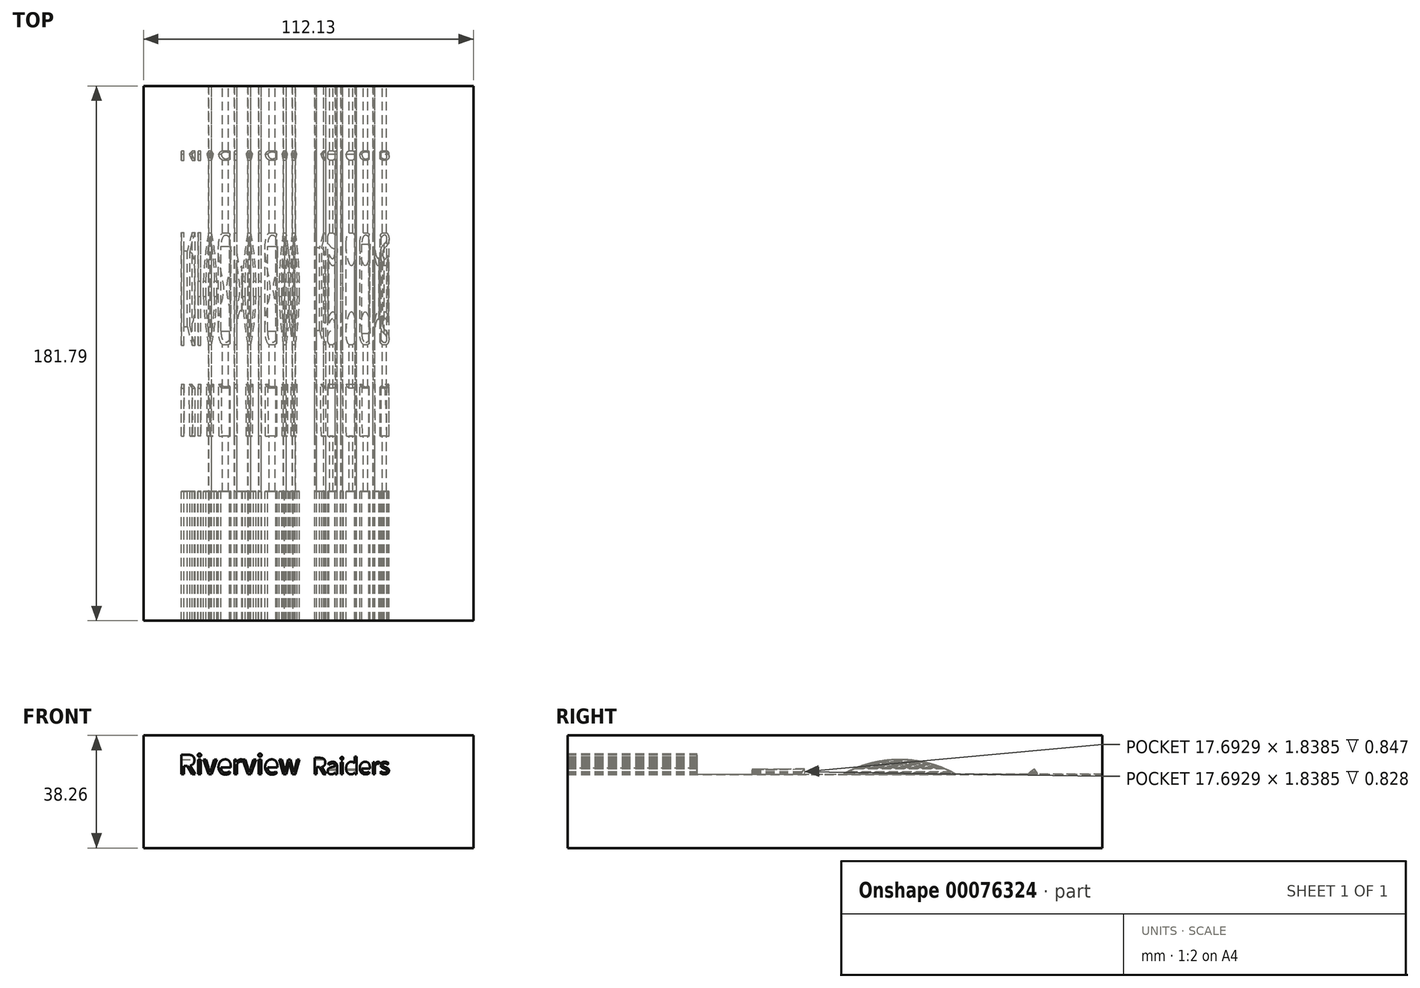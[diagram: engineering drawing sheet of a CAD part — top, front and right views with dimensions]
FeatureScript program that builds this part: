
annotation { "Feature Type Name" : "Feature", "Feature Type Description" : "" }
export const myFeature = defineFeature(function(context is Context, id is Id, definition is map)
    precondition{}
    {
        {
            var Q0;
            Q0=qCreatedBy(makeId("Front.planeOp"),FACE);
            var sketch = newSketch(context, id + "F0", { "sketchPlane" : qUnion([Q0])});
            skLineSegment(sketch, "E0.bottom", {"start": v(-57.39, 38.26) * mm, "end": v(54.74, 38.26) * mm});
            skLineSegment(sketch, "E0.top", {"start": v(-57.39, 0) * mm, "end": v(54.74, 0) * mm});
            skLineSegment(sketch, "E0.left", {"start": v(-57.39, 38.26) * mm, "end": v(-57.39, 0) * mm});
            skLineSegment(sketch, "E0.right", {"start": v(54.74, 38.26) * mm, "end": v(54.74, 0) * mm});
            skSolve(sketch);
        }
        {
            var Q0;
            Q0=makeQuery(id+"F0.imprint","IMPRINT",FACE,{"disambiguationData":[TD([[makeQuery(id+"F0.imprint","IMPRINT",EDGE,{"derivedFrom":sQuery(id+"F0.wireOp",EDGE,"E0.bottom")}),-1.0]])]});
            extrude(context, id + "F1", {"entities" : qUnion([Q0]), "depth" : 137.87 * mm});
        }
        {
            var Q0;
            Q0=makeQuery(id+"F1.opExtrude","CAP_FACE",FACE,{"disambiguationData":[OSD([sQuery(id+"F0.wireOp",EDGE,"E0.bottom"),sQuery(id+"F0.wireOp",EDGE,"E0.top"),sQuery(id+"F0.wireOp",EDGE,"E0.left"),sQuery(id+"F0.wireOp",EDGE,"E0.right")])],"isStart":false});
            var sketch = newSketch(context, id + "F2", { "sketchPlane" : qUnion([Q0])});
            skLineSegment(sketch, "E1.bottom", {"start": v(-35.27, 25.15) * mm, "end": v(33.51, 25.15) * mm});
            skLineSegment(sketch, "E1.top", {"start": v(-35.27, 0) * mm, "end": v(33.51, 0) * mm});
            skLineSegment(sketch, "E1.left", {"start": v(-35.27, 25.15) * mm, "end": v(-35.27, 0) * mm});
            skLineSegment(sketch, "E1.right", {"start": v(33.51, 25.15) * mm, "end": v(33.51, 0) * mm});
            skSolve(sketch);
        }
        {
            var Q0;
            Q0=makeQuery(id+"F2.imprint","IMPRINT",FACE,{"disambiguationData":[TD([[makeQuery(id+"F2.imprint","IMPRINT",EDGE,{"derivedFrom":sQuery(id+"F2.wireOp",EDGE,"E1.bottom")}),-1.0]])]});
            extrude(context, id + "F3", {"entities" : qUnion([Q0]), "operationType" : NewBodyOperationType.REMOVE, "endBound" : BoundingType.THROUGH_ALL, "oppositeDirection" : true, "depth" : 25.4 * mm});
        }
        {
            var Q0;
            Q0=makeQuery(id+"F1.opExtrude","SWEPT_FACE",FACE,{"disambiguationData":[OSD([sQuery(id+"F0.wireOp",EDGE,"E0.right")])]});
            var sketch = newSketch(context, id + "F4", { "sketchPlane" : qUnion([Q0])});
            skCircle(sketch, "E2", {"center": v(-128.5, 9.13) * mm, "radius": 2.38 * mm});
            skSolve(sketch);
        }
        {
            var Q0;
            Q0=makeQuery(id+"F4.imprint","IMPRINT",FACE,{"disambiguationData":[TD([[makeQuery(id+"F4.imprint","IMPRINT",EDGE,{"derivedFrom":sQuery(id+"F4.wireOp",EDGE,"E2")}),1.0]])]});
            extrude(context, id + "F5", {"entities" : qUnion([Q0]), "operationType" : NewBodyOperationType.REMOVE, "endBound" : BoundingType.THROUGH_ALL, "oppositeDirection" : true, "depth" : 25.4 * mm});
        }
        {
            var Q0;
            Q0=makeQuery(id+"F1.opExtrude","SWEPT_FACE",FACE,{"disambiguationData":[OSD([sQuery(id+"F0.wireOp",EDGE,"E0.right")])]});
            var sketch = newSketch(context, id + "F6", { "sketchPlane" : qUnion([Q0])});
            skCircle(sketch, "E3", {"center": v(-6.5, 4.13) * mm, "radius": 2.38 * mm});
            skSolve(sketch);
        }
        {
            var Q0;
            Q0=makeQuery(id+"F6.imprint","IMPRINT",FACE,{"disambiguationData":[TD([[makeQuery(id+"F6.imprint","IMPRINT",EDGE,{"derivedFrom":sQuery(id+"F6.wireOp",EDGE,"E3")}),1.0]])]});
            extrude(context, id + "F7", {"entities" : qUnion([Q0]), "operationType" : NewBodyOperationType.REMOVE, "endBound" : BoundingType.THROUGH_ALL, "oppositeDirection" : true, "depth" : 25.4 * mm});
        }
        {
            var Q0;
            Q0=makeQuery(id+"F1.opExtrude","SWEPT_FACE",FACE,{"disambiguationData":[OSD([sQuery(id+"F0.wireOp",EDGE,"E0.right")])]});
            var sketch = newSketch(context, id + "F8", { "sketchPlane" : qUnion([Q0])});
            skCircle(sketch, "E4", {"center": v(-68.94, -8.9) * mm, "radius": 39 * mm});
            skPoint(sketch, "E4.centerSnap0", {"position": v(-68.94, 0) * mm});
            skSolve(sketch);
        }
        {
            var Q0;
            {var subQ0=sQuery(id+"F8.wireOp",EDGE,"E4");var subQ1=makeQuery(id+"F1.opExtrude","SWEPT_EDGE",EDGE,{"disambiguationData":[OSD([sQuery(id+"F0.wireOp",EDGE,"E0.top"),sQuery(id+"F0.wireOp",EDGE,"E0.right")])]});var subQ2=makeQuery(id+"F8.imprint","INTERSECT",VERTEX,{"disambiguationData":[OD(0.0)],"derivedFrom":[subQ1,subQ0]});Q0=makeQuery(id+"F8.imprint","IMPRINT",FACE,{"disambiguationData":[TD([[makeQuery(id+"F8.imprint","IMPRINT",EDGE,{"disambiguationData":[TD([[subQ2,-1.0]])],"derivedFrom":subQ0}),1.0]])]});}
            extrude(context, id + "F9", {"entities" : qUnion([Q0]), "operationType" : NewBodyOperationType.REMOVE, "endBound" : BoundingType.THROUGH_ALL, "oppositeDirection" : true, "depth" : 25.4 * mm});
        }
        {
            var Q0;
            Q0=makeQuery(id+"F1.opExtrude","SWEPT_FACE",FACE,{"disambiguationData":[OSD([sQuery(id+"F0.wireOp",EDGE,"E0.right")])]});
            var sketch = newSketch(context, id + "F10", { "sketchPlane" : qUnion([Q0])});
            skArc(sketch, "E5", {"start": v(-23.1, 26.79) * mm, "mid": v(-26, 16.4) * mm, "end": v(-15.49, 14.04) * mm});
            skPoint(sketch, "E5.endSnap0", {"position": v(-15.49, 0) * mm});
            skLineSegment(sketch, "E6", {"start": v(-23.1, 26.79) * mm, "end": v(-15.49, 14.04) * mm});
            skSolve(sketch);
        }
        {
            var Q0;
            Q0=makeQuery(id+"F10.imprint","IMPRINT",FACE,{"disambiguationData":[TD([[makeQuery(id+"F10.imprint","IMPRINT",EDGE,{"derivedFrom":sQuery(id+"F10.wireOp",EDGE,"E5")}),1.0]])]});
            extrude(context, id + "F11", {"entities" : qUnion([Q0]), "operationType" : NewBodyOperationType.REMOVE, "endBound" : BoundingType.THROUGH_ALL, "oppositeDirection" : true, "depth" : 25.4 * mm});
        }
        {
            var Q0;
            Q0=makeQuery(id+"F1.opExtrude","SWEPT_FACE",FACE,{"disambiguationData":[OSD([sQuery(id+"F0.wireOp",EDGE,"E0.right")])]});
            var sketch = newSketch(context, id + "F12", { "sketchPlane" : qUnion([Q0])});
            skLineSegment(sketch, "E7", {"start": v(-119, 26.46) * mm, "end": v(-119, 12.1) * mm});
            skLineSegment(sketch, "E8", {"start": v(-119, 12.1) * mm, "end": v(-112.82, 12.1) * mm});
            skLineSegment(sketch, "E9", {"start": v(-112.82, 12.1) * mm, "end": v(-101.31, 26.9) * mm});
            skLineSegment(sketch, "E10", {"start": v(-101.31, 26.9) * mm, "end": v(-119, 26.46) * mm});
            skSolve(sketch);
        }
        {
            var Q0;
            Q0=makeQuery(id+"F12.imprint","IMPRINT",FACE,{"disambiguationData":[TD([[makeQuery(id+"F12.imprint","IMPRINT",EDGE,{"derivedFrom":sQuery(id+"F12.wireOp",EDGE,"E7")}),1.0]])]});
            extrude(context, id + "F13", {"entities" : qUnion([Q0]), "operationType" : NewBodyOperationType.REMOVE, "endBound" : BoundingType.THROUGH_ALL, "oppositeDirection" : true, "depth" : 25.4 * mm});
        }
        {
            var Q0;
            Q0=makeQuery(id+"F0.imprint","IMPRINT",FACE,{"disambiguationData":[TD([[makeQuery(id+"F0.imprint","IMPRINT",EDGE,{"derivedFrom":sQuery(id+"F0.wireOp",EDGE,"E0.bottom")}),-1.0]])]});
            var sketch = newSketch(context, id + "F14", { "sketchPlane" : qUnion([Q0])});
            skText(sketch, "E11", { "text": "Riverview", "fontName": "NotoSansCJKsc-Regular.otf"});
            skText(sketch, "E12", { "text": "Raiders", "fontName": "NotoSansCJKsc-Regular.otf"});
            const initialGuessF14  = {"E11": [-0.04543, 0.02506, 1, 0, 0.00656], "E12": [0, 0.02513, 1, 0, 0.0054]};
            skSetInitialGuess(sketch, initialGuessF14);
            skSolve(sketch);
        }
        {
            var Q0;
            Q0=makeQuery(id+"F14.imprint","IMPRINT",FACE,{"disambiguationData":[TD([[makeQuery(id+"F14.imprint","IMPRINT",EDGE,{"derivedFrom":sQuery(id+"F14.wireOp",EDGE,"E11.sketch_text.stroke-5")}),-1.0]])]});
            extrude(context, id + "F15", {"entities" : qUnion([Q0]), "operationType" : NewBodyOperationType.ADD, "endBound" : BoundingType.THROUGH_ALL, "depth" : 25.4 * mm});
        }
    });
